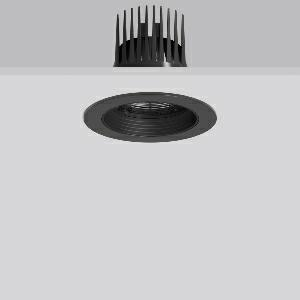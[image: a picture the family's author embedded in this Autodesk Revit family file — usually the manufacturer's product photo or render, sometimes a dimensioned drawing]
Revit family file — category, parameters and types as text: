
# Revit family: heledon_maxi_e_901768_003_95ca
name_source: partatom
category: Lighting Fixtures
units: mm (PartAtom-declared; Revit-internal decimal feet)

## family parameters
Cut with Voids When Loaded = No
Host = Face
Light Source = No
Part Type = Normal
Room Calculation Point = No
Round Connector Dimension = Use Diameter
Shared = No

## types (1)
- HELEDON maxi E (1 x LED Modul 930, 3500 lm, 3000)
    Apparent Load = 35 VA
    Approval mark = CE
    CIE Flux Codes = 96 100 100 100 100
    Color Rendering = 90
    Color Temperature = 3000
    Default Elevation = 1800 mm
    Description = Series: HELEDON maxi
Round recessed downlight. Housing: die-cast aluminium, powder-coated. Black plastic ring and recessed LED to prevent glare from the side. Optical assembly with lens made of plastic (polycarbonate) for the best homogeneous light distribution - can be changed without tools. Best colour rendering index Ra>90. Suitable for Recessed ceiling mounting. Installation without tools thanks to spring fastening system. Including separate LED converter with connecting cable 600 mm.High quality converter without flickering and stroboscopic effect. Through-wiring box (5 pole) available as accessory. The following accessories can be mounted without use of tools: interchangeable lenses, decorative glasses, honeycomb louvre, clear and frosted diffusers, white interchangeable plastic ring. 
Colour: deep black, matt (RAL 9005)
Diameter: 162 mm
Height: 3 mm
Cut-out diameter: 152 mm
Recess height: 200 mm
Luminaire: recess height: 135 mm
Lamp: LED
Socket: without socket
Colour temperature: 3000K
Colour rendering index (CRI): 92
System power: 35 W
Rated luminous flux: 3500 lm
Luminous efficiency: 100 lm/W
Control gear: Regulated power supply
Protection class: II
Type of protection: IP 20
    Height = 0 mm  [stored 0 ft]
    Lamp = 1 x LED Modul 930
    Lamp Light Flux = 3500 lm
    Lamp count = 1
    Length = 162 mm
    Lifetime = 50000 h
    Luminous efficacy = 100 lm/W
    Manufacturer = RZB
    ModVariant = No
    Model = 901768.003
    Mounting Place = Ceiling
    Mounting Type = Recessed
    Number of Poles = 1
    OnlyDefault = Yes
    Power Factor = 1
    Product Name = HELEDON maxi E
    Product group = Recessed downlights
    ProductGroupID = 402
    Protection Class = Protection class II
    Protection Degree = IP 20
    RLX_Detail_Level = 1
    RLX_Emergency_Light_Flux = 0 lm
    RLX_Emergency_Type = 0
    RLX_Emergency_Type_DB = No
    RlxData = <blob elided: 120933 chars, md5=8b8b9f1a>
    Socket = socket
    Standby Power = 0 W
    System Light Flux = 3500 lm
    System Power = 35 W
    Type Comments = Product without accessories
    Type Image = 901663.003.jpg
    URL = http://relux.com
    VarID = ---
    Voltage = 230 V
    Voltage Range = 220-240 V
    Weight = 0.00 kg
    Width = 0 mm  [stored 0 ft]

note: [stored X ft] marks values corroborated as IEEE doubles in the binary element streams (Revit-internal decimal feet)

## geometry (parser evidence)
native form markers: Blend x4, Sweep x12
no freeform markers — native parametric forms only
